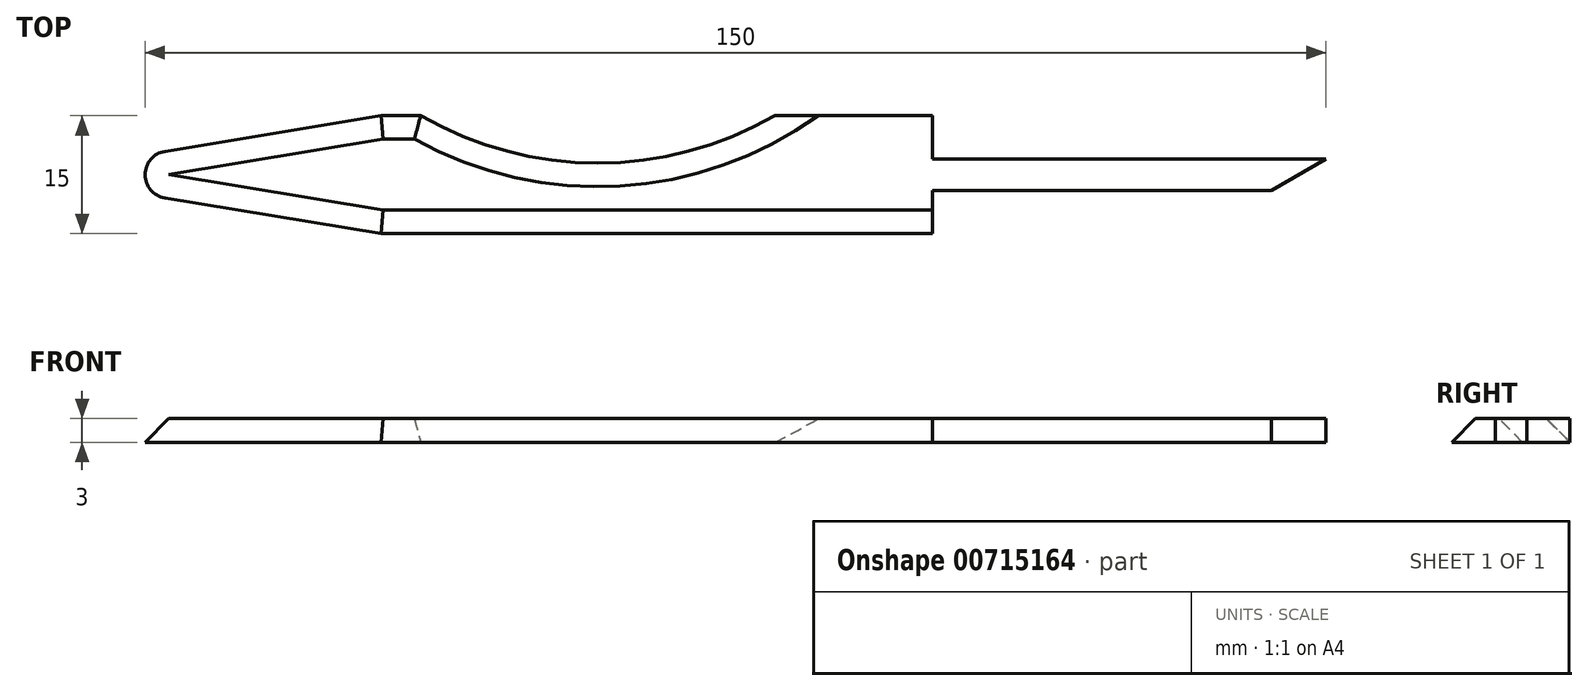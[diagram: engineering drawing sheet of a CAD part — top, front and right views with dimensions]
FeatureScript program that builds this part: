
annotation { "Feature Type Name" : "Feature", "Feature Type Description" : "" }
export const myFeature = defineFeature(function(context is Context, id is Id, definition is map)
    precondition{}
    {
        {
            var Q0;
            Q0=qCreatedBy(makeId("Top.planeOp"),FACE);
            var sketch = newSketch(context, id + "F0", { "sketchPlane" : qUnion([Q0])});
            skLineSegment(sketch, "E0", {"start": v(0, 7.5) * mm, "end": v(-20, 7.5) * mm});
            skLineSegment(sketch, "E1", {"start": v(0, -7.5) * mm, "end": v(-70, -7.5) * mm});
            skLineSegment(sketch, "E2", {"start": v(-70, -7.5) * mm, "end": v(-97.49, -2.96) * mm});
            skLineSegment(sketch, "E3", {"start": v(-97.49, 2.96) * mm, "end": v(-70, 7.5) * mm});
            skLineSegment(sketch, "E4", {"start": v(-70, -7.5) * mm, "end": v(-70, 7.5) * mm});
            skLineSegment(sketch, "E5", {"start": v(-100, 0) * mm, "end": v(-70, 0) * mm});
            skLineSegment(sketch, "E6", {"start": v(0, 7.5) * mm, "end": v(0, 0) * mm});
            skLineSegment(sketch, "E7", {"start": v(0, 0) * mm, "end": v(0, -7.5) * mm});
            skLineSegment(sketch, "E8", {"start": v(-70, 7.5) * mm, "end": v(-65, 7.5) * mm});
            skArc(sketch, "E9", {"start": v(-65, 7.5) * mm, "mid": v(-42.5, 1.47) * mm, "end": v(-20, 7.5) * mm});
            skLineSegment(sketch, "E10", {"start": v(50, 2) * mm, "end": v(0, 2) * mm});
            skLineSegment(sketch, "E11", {"start": v(50, 2) * mm, "end": v(43.07, -2) * mm});
            skArc(sketch, "E12.filletArc", {"start": v(-97.49, 2.96) * mm, "mid": v(-100, 0) * mm, "end": v(-97.49, -2.96) * mm});
            skLineSegment(sketch, "E13", {"start": v(43.07, -2) * mm, "end": v(0, -2) * mm});
            skSolve(sketch);
        }
        {
            var Q0;
            Q0 = qSketchRegion(id + "F0", true);
            extrude(context, id + "F1", {"entities" : qUnion([Q0]), "depth" : 3 * mm, "offsetDistance" : 25 * mm});
        }
        {
            var Q0;
            Q0=makeQuery(id+"F1.opExtrude","CAP_EDGE",EDGE,{"disambiguationData":[OSD([sQuery(id+"F0.wireOp",EDGE,"E9")])],"isStart":false});
            var Q1;
            Q1=makeQuery(id+"F1.opExtrude","CAP_EDGE",EDGE,{"disambiguationData":[OSD([sQuery(id+"F0.wireOp",EDGE,"E3")])],"isStart":false});
            var Q2;
            Q2=makeQuery(id+"F1.opExtrude","CAP_EDGE",EDGE,{"disambiguationData":[OSD([sQuery(id+"F0.wireOp",EDGE,"E8")])],"isStart":false});
            var Q3;
            Q3=makeQuery(id+"F1.opExtrude","CAP_EDGE",EDGE,{"disambiguationData":[OSD([sQuery(id+"F0.wireOp",EDGE,"E12.filletArc")])],"isStart":false});
            var Q4;
            Q4=makeQuery(id+"F1.opExtrude","CAP_EDGE",EDGE,{"disambiguationData":[OSD([sQuery(id+"F0.wireOp",EDGE,"E2")])],"isStart":false});
            var Q5;
            Q5=makeQuery(id+"F1.opExtrude","CAP_EDGE",EDGE,{"disambiguationData":[OSD([sQuery(id+"F0.wireOp",EDGE,"E1")])],"isStart":false});
            chamfer(context, id + "F2", {"entities" : qUnion([Q0, Q1, Q2, Q3, Q4, Q5]), "width" : 3 * mm});
        }
    });
